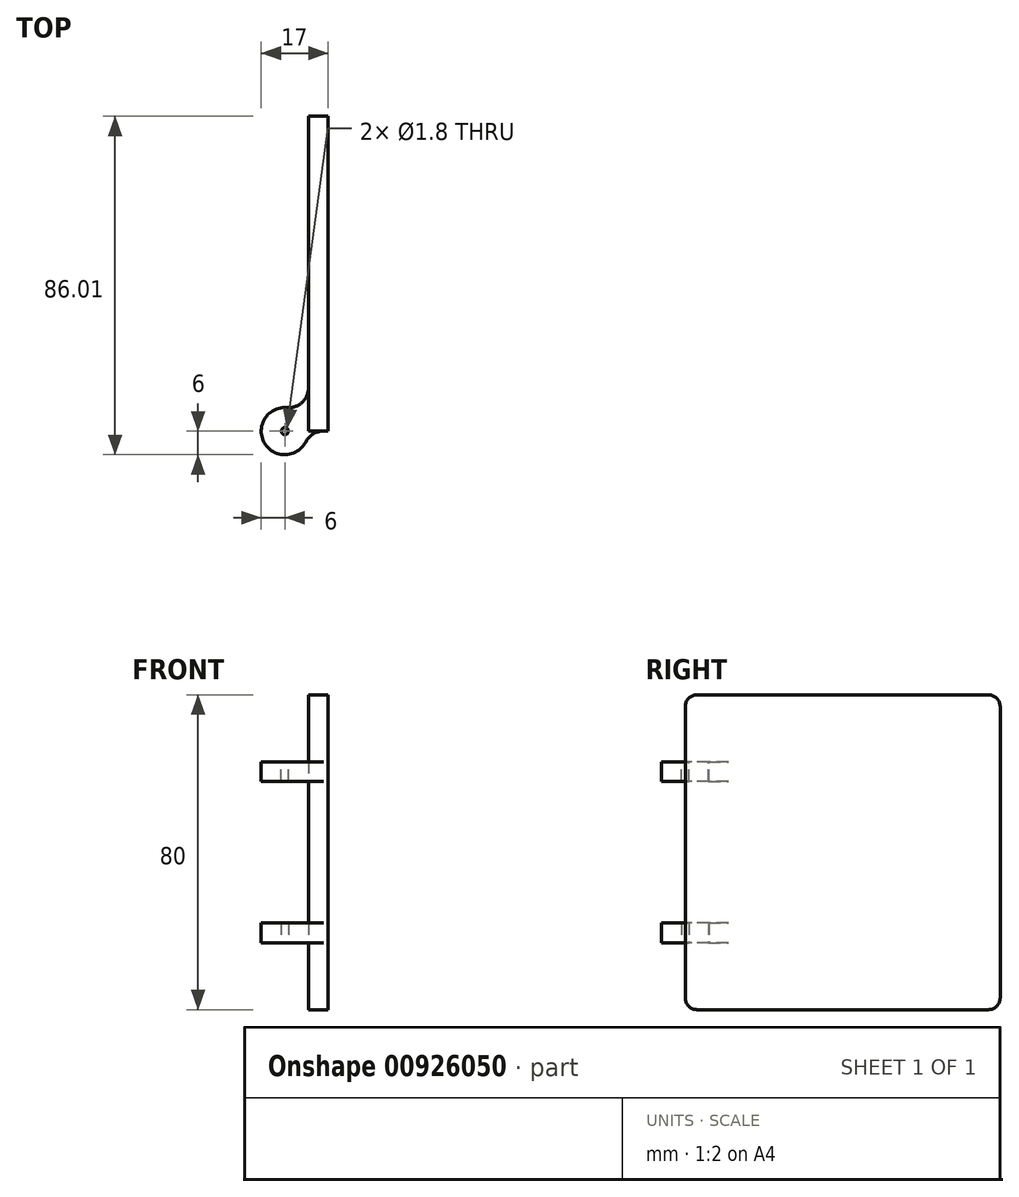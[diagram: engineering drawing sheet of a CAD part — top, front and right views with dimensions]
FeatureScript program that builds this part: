
annotation { "Feature Type Name" : "Feature", "Feature Type Description" : "" }
export const myFeature = defineFeature(function(context is Context, id is Id, definition is map)
    precondition{}
    {
        {
            var Q0;
            Q0=qCreatedBy(makeId("Top.planeOp"),FACE);
            var sketch = newSketch(context, id + "F0", { "sketchPlane" : qUnion([Q0])});
            skCircle(sketch, "E0", {"center": v(0, 0) * mm, "radius": 6 * mm});
            skCircle(sketch, "E1", {"center": v(0, 0) * mm, "radius": 0.9 * mm});
            skSolve(sketch);
        }
        {
            var Q0;
            Q0=makeQuery(id+"F0.imprint","IMPRINT",FACE,{"disambiguationData":[TD([[makeQuery(id+"F0.imprint","IMPRINT",EDGE,{"derivedFrom":sQuery(id+"F0.wireOp",EDGE,"E0")}),1.0]])]});
            extrude(context, id + "F1", {"entities" : qUnion([Q0]), "depth" : 5 * mm, "offsetDistance" : 25 * mm});
        }
        {
            var Q0;
            Q0=qCreatedBy(makeId("Top.planeOp"),FACE);
            cPlane(context, id + "F2", {"entities" : qUnion([Q0]), "cplaneType" : CPlaneType.OFFSET, "offset" : 46 * mm, "width" : 150 * mm, "height" : 150 * mm});
        }
        {
            var Q0;
            Q0=qCreatedBy(id+"F2.planeOp",FACE);
            var sketch = newSketch(context, id + "F3", { "sketchPlane" : qUnion([Q0])});
            skCircle(sketch, "E2", {"center": v(0, 0) * mm, "radius": 6 * mm});
            skCircle(sketch, "E3", {"center": v(0, 0) * mm, "radius": 0.9 * mm});
            skSolve(sketch);
        }
        {
            var Q0;
            Q0=qSketchRegion(id+"F3",true);
            var Q1;
            Q1=makeQuery(id+"F3.imprint","IMPRINT",FACE,{"disambiguationData":[TD([[makeQuery(id+"F3.imprint","IMPRINT",EDGE,{"derivedFrom":sQuery(id+"F3.wireOp",EDGE,"E2")}),1.0]])]});
            extrude(context, id + "F4", {"entities" : qUnion([Q0, Q1]), "oppositeDirection" : true, "depth" : 5 * mm, "offsetDistance" : 25 * mm});
        }
        {
            var Q0;
            Q0=qCreatedBy(makeId("Top.planeOp"),FACE);
            var sketch = newSketch(context, id + "F5", { "sketchPlane" : qUnion([Q0])});
            skLineSegment(sketch, "E4", {"start": v(6, 0.01) * mm, "end": v(6, 80.01) * mm});
            skLineSegment(sketch, "E5", {"start": v(6, 80.01) * mm, "end": v(11, 80.01) * mm});
            skLineSegment(sketch, "E6", {"start": v(11, 80.01) * mm, "end": v(11, 0.01) * mm});
            skLineSegment(sketch, "E7", {"start": v(11, 0.01) * mm, "end": v(6, 0.01) * mm});
            skSolve(sketch);
        }
        {
            var Q0;
            Q0=makeQuery(id+"F5.imprint","IMPRINT",FACE,{"disambiguationData":[TD([[makeQuery(id+"F5.imprint","IMPRINT",EDGE,{"derivedFrom":sQuery(id+"F5.wireOp",EDGE,"E4")}),-1.0]])]});
            extrude(context, id + "F6", {"entities" : qUnion([Q0]), "operationType" : NewBodyOperationType.ADD, "depth" : 63 * mm, "offsetDistance" : 25 * mm, "hasSecondDirection" : true, "secondDirectionOppositeDirection" : true, "secondDirectionDepth" : 17 * mm});
        }
        {
            var Q0;
            Q0=makeQuery(id+"F6.boolean.opBoolean","INTERSECT",EDGE,{"derivedFrom":[makeQuery(id+"F4.opExtrude","SWEPT_FACE",FACE,{"disambiguationData":[OSD([sQuery(id+"F3.wireOp",EDGE,"E2")])]}),makeQuery(id+"F6.opExtrude","SWEPT_FACE",FACE,{"disambiguationData":[OSD([sQuery(id+"F5.wireOp",EDGE,"E4")])]})]});
            var Q1;
            Q1=makeQuery(id+"F6.boolean.opBoolean","INTERSECT",EDGE,{"derivedFrom":[makeQuery(id+"F1.opExtrude","SWEPT_FACE",FACE,{"disambiguationData":[OSD([sQuery(id+"F0.wireOp",EDGE,"E0")])]}),makeQuery(id+"F6.opExtrude","SWEPT_FACE",FACE,{"disambiguationData":[OSD([sQuery(id+"F5.wireOp",EDGE,"E4")])]})]});
            var Q2;
            Q2=makeQuery(id+"F6.boolean.opBoolean","INTERSECT",EDGE,{"derivedFrom":[makeQuery(id+"F1.opExtrude","SWEPT_FACE",FACE,{"disambiguationData":[OSD([sQuery(id+"F0.wireOp",EDGE,"E0")])]}),makeQuery(id+"F6.opExtrude","SWEPT_FACE",FACE,{"disambiguationData":[OSD([sQuery(id+"F5.wireOp",EDGE,"E7")])]})]});
            var Q3;
            Q3=makeQuery(id+"F6.boolean.opBoolean","INTERSECT",EDGE,{"derivedFrom":[makeQuery(id+"F4.opExtrude","SWEPT_FACE",FACE,{"disambiguationData":[OSD([sQuery(id+"F3.wireOp",EDGE,"E2")])]}),makeQuery(id+"F6.opExtrude","SWEPT_FACE",FACE,{"disambiguationData":[OSD([sQuery(id+"F5.wireOp",EDGE,"E7")])]})]});
            fillet(context, id + "F7", {"entities" : qUnion([Q0, Q1, Q2, Q3]), "radius" : 5 * mm, "tangentPropagation" : true, "allowEdgeOverflow" : false});
        }
        {
            var Q0;
            Q0=makeQuery(id+"F6.opExtrude","CAP_EDGE",EDGE,{"disambiguationData":[OSD([sQuery(id+"F5.wireOp",EDGE,"E5")])],"isStart":false});
            var Q1;
            Q1=makeQuery(id+"F6.opExtrude","CAP_EDGE",EDGE,{"disambiguationData":[OSD([sQuery(id+"F5.wireOp",EDGE,"E7")])],"isStart":false});
            var Q2;
            Q2=makeQuery(id+"F6.opExtrude","CAP_EDGE",EDGE,{"disambiguationData":[OSD([sQuery(id+"F5.wireOp",EDGE,"E5")])],"isStart":true});
            var Q3;
            Q3=makeQuery(id+"F6.opExtrude","CAP_EDGE",EDGE,{"disambiguationData":[OSD([sQuery(id+"F5.wireOp",EDGE,"E7")])],"isStart":true});
            fillet(context, id + "F8", {"entities" : qUnion([Q0, Q1, Q2, Q3]), "radius" : 3 * mm, "tangentPropagation" : true, "allowEdgeOverflow" : false});
        }
    });
